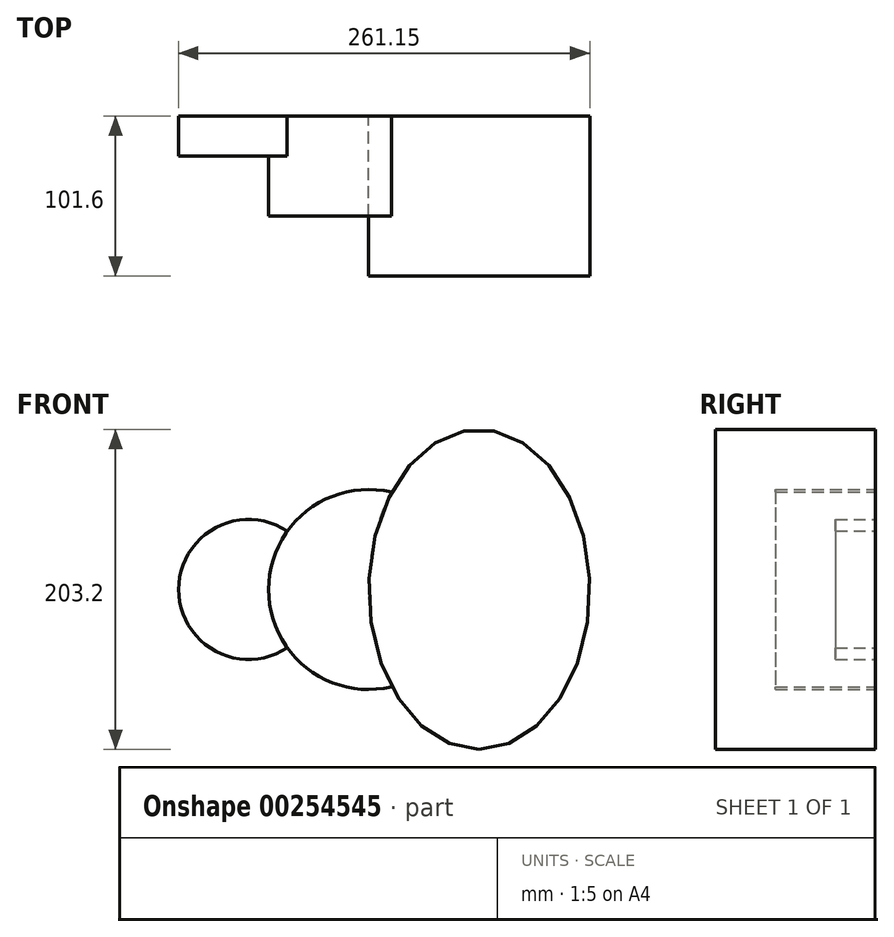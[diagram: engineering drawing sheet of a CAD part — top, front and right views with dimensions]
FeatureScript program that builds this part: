
annotation { "Feature Type Name" : "Feature", "Feature Type Description" : "" }
export const myFeature = defineFeature(function(context is Context, id is Id, definition is map)
    precondition{}
    {
        {
            var Q0;
            Q0=qCreatedBy(makeId("Front.planeOp"),FACE);
            var sketch = newSketch(context, id + "F0", { "sketchPlane" : qUnion([Q0])});
            skCircle(sketch, "E0", {"center": v(-76.2, 0) * mm, "radius": 44.45 * mm});
            skCircle(sketch, "E1", {"center": v(0, 0) * mm, "radius": 63.5 * mm});
            skPoint(sketch, "E2", {"position": v(-63.5, 0) * mm});
            skPoint(sketch, "E3", {"position": v(-31.75, 0) * mm});
            skEllipse(sketch, "E4", {"center": v(70.25, 0) * mm, "majorRadius": 70.25 * mm, "minorRadius": 101.6 * mm, "majorAxis": v(-1, 0)});
            skPoint(sketch, "E5", {"position": v(70.25, 101.6) * mm});
            skSolve(sketch);
        }
        {
            var Q0;
            {var subQ0=sQuery(id+"F0.wireOp",EDGE,"E1");var subQ1=sQuery(id+"F0.wireOp",EDGE,"E0");var subQ2=makeQuery(id+"F0.imprint","INTERSECT",VERTEX,{"disambiguationData":[OD(0.0)],"derivedFrom":[subQ1,subQ0]});Q0=makeQuery(id+"F0.imprint","IMPRINT",FACE,{"disambiguationData":[TD([[makeQuery(id+"F0.imprint","IMPRINT",EDGE,{"disambiguationData":[TD([[subQ2,-1.0]])],"derivedFrom":subQ1}),1.0]])]});}
            extrude(context, id + "F1", {"entities" : qUnion([Q0]), "depth" : 25.4 * mm});
        }
        {
            var Q0;
            {var subQ0=sQuery(id+"F0.wireOp",EDGE,"E1");var subQ1=sQuery(id+"F0.wireOp",EDGE,"E0");var subQ2=makeQuery(id+"F0.imprint","INTERSECT",VERTEX,{"disambiguationData":[OD(0.0)],"derivedFrom":[subQ1,subQ0]});Q0=makeQuery(id+"F0.imprint","IMPRINT",FACE,{"disambiguationData":[TD([[makeQuery(id+"F0.imprint","IMPRINT",EDGE,{"disambiguationData":[TD([[subQ2,1.0]])],"derivedFrom":subQ1}),1.0]])]});}
            var Q1;
            {var subQ0=sQuery(id+"F0.wireOp",EDGE,"E1");var subQ1=sQuery(id+"F0.wireOp",EDGE,"E0");var subQ2=makeQuery(id+"F0.imprint","INTERSECT",VERTEX,{"disambiguationData":[OD(0.0)],"derivedFrom":[subQ1,subQ0]});Q1=makeQuery(id+"F0.imprint","IMPRINT",FACE,{"disambiguationData":[TD([[makeQuery(id+"F0.imprint","IMPRINT",EDGE,{"disambiguationData":[TD([[subQ2,1.0]])],"derivedFrom":subQ1}),-1.0]])]});}
            extrude(context, id + "F2", {"entities" : qUnion([Q0, Q1]), "operationType" : NewBodyOperationType.ADD, "depth" : 63.5 * mm});
        }
        {
            var Q0;
            {var subQ0=sQuery(id+"F0.wireOp",EDGE,"E4");var subQ1=sQuery(id+"F0.wireOp",EDGE,"E1");var subQ2=makeQuery(id+"F0.imprint","INTERSECT",VERTEX,{"disambiguationData":[OD(0.0)],"derivedFrom":[subQ1,subQ0]});Q0=makeQuery(id+"F0.imprint","IMPRINT",FACE,{"disambiguationData":[TD([[makeQuery(id+"F0.imprint","IMPRINT",EDGE,{"disambiguationData":[TD([[subQ2,1.0]])],"derivedFrom":subQ1}),1.0]])]});}
            var Q1;
            {var subQ0=sQuery(id+"F0.wireOp",EDGE,"E4");var subQ1=sQuery(id+"F0.wireOp",EDGE,"E1");var subQ2=makeQuery(id+"F0.imprint","INTERSECT",VERTEX,{"disambiguationData":[OD(0.0)],"derivedFrom":[subQ1,subQ0]});Q1=makeQuery(id+"F0.imprint","IMPRINT",FACE,{"disambiguationData":[TD([[makeQuery(id+"F0.imprint","IMPRINT",EDGE,{"disambiguationData":[TD([[subQ2,1.0]])],"derivedFrom":subQ1}),-1.0]])]});}
            extrude(context, id + "F3", {"entities" : qUnion([Q0, Q1]), "depth" : 101.6 * mm});
        }
    });
